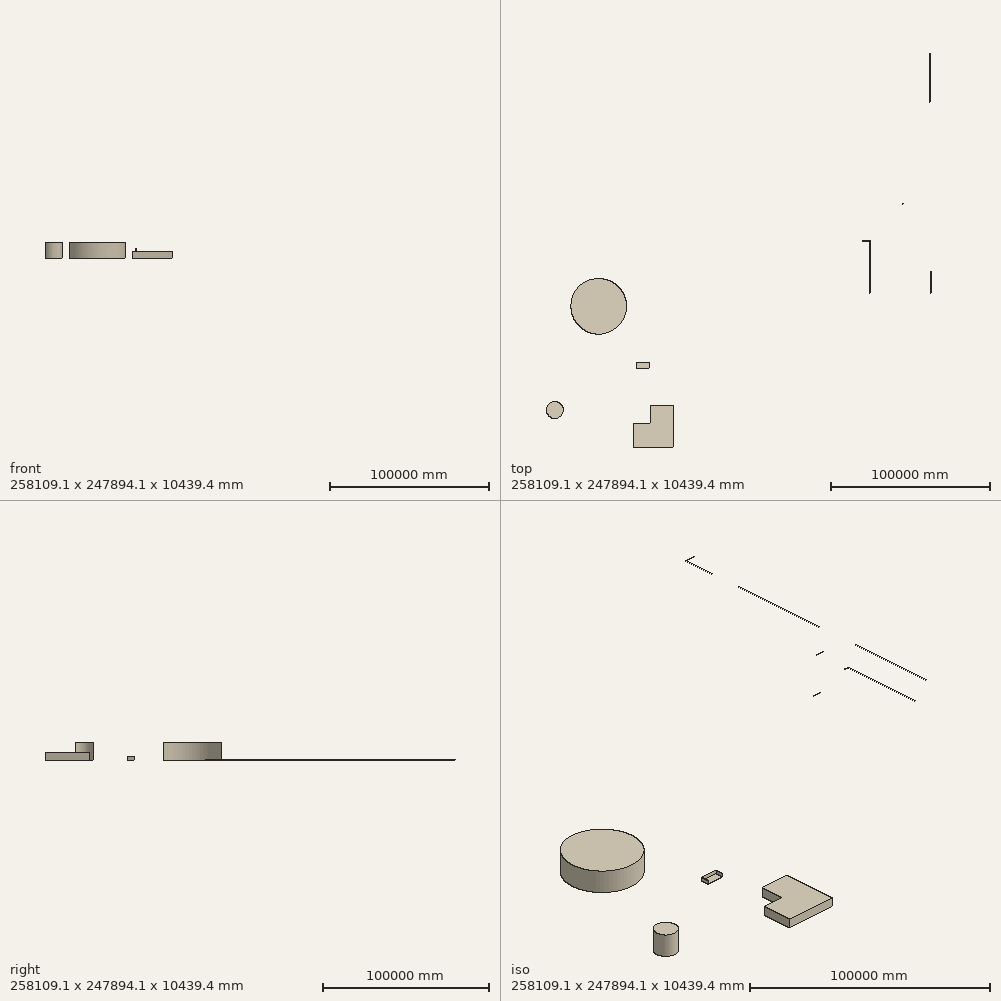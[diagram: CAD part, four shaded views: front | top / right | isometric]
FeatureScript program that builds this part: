
annotation { "Feature Type Name" : "Feature", "Feature Type Description" : "" }
export const myFeature = defineFeature(function(context is Context, id is Id, definition is map)
    precondition{}
    {
        {
            var Q0;
            Q0=qCreatedBy(makeId("Top.planeOp"),FACE);
            var sketch = newSketch(context, id + "F0", { "sketchPlane" : qUnion([Q0])});
            skCircle(sketch, "E0", {"center": v(-50054.64, -23220.98) * mm, "radius": 5334 * mm});
            skCircle(sketch, "E1", {"center": v(-35519.36, -23220.98) * mm, "radius": 5334 * mm});
            skCircle(sketch, "E2", {"center": v(-21108.4, -23220.98) * mm, "radius": 5334 * mm});
            skLineSegment(sketch, "E3", {"start": v(-70389.93, -5352.59) * mm, "end": v(-70389.93, -40568.15) * mm});
            skLineSegment(sketch, "E4", {"start": v(-68865.93, -3828.59) * mm, "end": v(-2745.86, -3828.59) * mm});
            skLineSegment(sketch, "E5", {"start": v(-1222.92, -5409.41) * mm, "end": v(-2607.68, -42521) * mm});
            skLineSegment(sketch, "E6", {"start": v(-68910.55, -42091.5) * mm, "end": v(-4175.24, -43987.52) * mm});
            skPoint(sketch, "E7.visualSharp", {"position": v(-70389.93, -3828.59) * mm});
            skArc(sketch, "E7.filletArc", {"start": v(-68865.93, -3828.59) * mm, "mid": v(-69943.56, -4274.96) * mm, "end": v(-70389.93, -5352.59) * mm});
            skPoint(sketch, "E8.visualSharp", {"position": v(-70389.93, -42048.17) * mm});
            skArc(sketch, "E8.filletArc", {"start": v(-70389.93, -40568.15) * mm, "mid": v(-69959.22, -41629.9) * mm, "end": v(-68910.55, -42091.5) * mm});
            skPoint(sketch, "E9.visualSharp", {"position": v(-2664.05, -44031.78) * mm});
            skArc(sketch, "E9.filletArc", {"start": v(-4175.24, -43987.52) * mm, "mid": v(-3089.45, -43577.07) * mm, "end": v(-2607.68, -42521) * mm});
            skPoint(sketch, "E10.visualSharp", {"position": v(-1163.93, -3828.59) * mm});
            skArc(sketch, "E10.filletArc", {"start": v(-1222.92, -5409.41) * mm, "mid": v(-1648.32, -4295.24) * mm, "end": v(-2745.86, -3828.59) * mm});
            skLineSegment(sketch, "E11", {"start": v(-50011.35, 72049.65) * mm, "end": v(-50011.35, 14325.6) * mm});
            skLineSegment(sketch, "E12", {"start": v(-50011.35, 14325.6) * mm, "end": v(35090.4, 14325.6) * mm});
            skLineSegment(sketch, "E13", {"start": v(35090.4, 14325.6) * mm, "end": v(35090.4, 75018.32) * mm});
            skLineSegment(sketch, "E14", {"start": v(35090.4, 75018.32) * mm, "end": v(27173.95, 75018.32) * mm});
            skLineSegment(sketch, "E15", {"start": v(27173.95, 75018.32) * mm, "end": v(27173.95, 93160.17) * mm});
            skLineSegment(sketch, "E16", {"start": v(27173.95, 93160.17) * mm, "end": v(-3007.48, 93160.17) * mm});
            skLineSegment(sketch, "E17", {"start": v(-3007.48, 93160.17) * mm, "end": v(-3007.48, 72049.65) * mm});
            skLineSegment(sketch, "E18", {"start": v(-3007.48, 72049.65) * mm, "end": v(-50011.35, 72049.65) * mm});
            skLineSegment(sketch, "E19.bottom", {"start": v(-57326.54, 5607.47) * mm, "end": v(41719.62, 5607.47) * mm});
            skLineSegment(sketch, "E19.top", {"start": v(-11431.89, 100338.75) * mm, "end": v(41719.62, 100338.75) * mm});
            skLineSegment(sketch, "E19.left", {"start": v(-57326.54, 5607.47) * mm, "end": v(-57326.54, 78356.48) * mm});
            skLineSegment(sketch, "E19.right", {"start": v(41719.62, 5607.47) * mm, "end": v(41719.62, 100338.75) * mm});
            skLineSegment(sketch, "E20", {"start": v(-11431.89, 100338.75) * mm, "end": v(-11431.89, 78356.48) * mm});
            skLineSegment(sketch, "E21", {"start": v(-11431.89, 78356.48) * mm, "end": v(-57326.54, 78356.48) * mm});
            skLineSegment(sketch, "E22", {"start": v(24636.78, -20086.42) * mm, "end": v(24636.78, -46694.1) * mm});
            skLineSegment(sketch, "E23", {"start": v(24636.78, -46694.1) * mm, "end": v(-445.33, -46694.1) * mm});
            skLineSegment(sketch, "E24", {"start": v(-445.33, -46694.1) * mm, "end": v(-445.33, -31842.26) * mm});
            skLineSegment(sketch, "E25", {"start": v(-445.33, -31842.26) * mm, "end": v(10009.28, -31842.26) * mm});
            skLineSegment(sketch, "E26", {"start": v(10009.28, -31842.26) * mm, "end": v(10009.28, -20086.42) * mm});
            skLineSegment(sketch, "E27", {"start": v(10009.28, -20086.42) * mm, "end": v(24636.78, -20086.42) * mm});
            skCircle(sketch, "E28", {"center": v(-22491.29, 42056.2) * mm, "radius": 17526 * mm});
            skLineSegment(sketch, "E29", {"start": v(-3866.35, 22739.19) * mm, "end": v(-2452.96, 22739.19) * mm});
            skLineSegment(sketch, "E30", {"start": v(-2452.96, 22739.19) * mm, "end": v(-2452.96, 6885.65) * mm});
            skLineSegment(sketch, "E31", {"start": v(-2452.96, 6885.65) * mm, "end": v(-3866.35, 6885.65) * mm});
            skLineSegment(sketch, "E32", {"start": v(-3866.35, 6885.65) * mm, "end": v(-3866.35, 9176.13) * mm});
            skLineSegment(sketch, "E33", {"start": v(-3866.35, 9176.13) * mm, "end": v(-55251.57, 10052.83) * mm});
            skLineSegment(sketch, "E34", {"start": v(-55251.57, 10052.83) * mm, "end": v(-55223.3, 11709.27) * mm});
            skLineSegment(sketch, "E35", {"start": v(-55223.3, 11709.27) * mm, "end": v(-3866.35, 10833.05) * mm});
            skLineSegment(sketch, "E36", {"start": v(-3866.35, 10833.05) * mm, "end": v(-3866.35, 22739.19) * mm});
            skSolve(sketch);
        }
        {
            var Q0;
            Q0=makeQuery(id+"F0.imprint","IMPRINT",FACE,{"disambiguationData":[TD([[makeQuery(id+"F0.imprint","IMPRINT",EDGE,{"derivedFrom":sQuery(id+"F0.wireOp",EDGE,"E28")}),1.0]])]});
            extrude(context, id + "F1", {"entities" : qUnion([Q0]), "depth" : 10363.2 * mm});
        }
        {
            var Q0;
            Q0=makeQuery(id+"F0.imprint","IMPRINT",FACE,{"disambiguationData":[TD([[makeQuery(id+"F0.imprint","IMPRINT",EDGE,{"derivedFrom":sQuery(id+"F0.wireOp",EDGE,"E0")}),1.0]])]});
            extrude(context, id + "F2", {"entities" : qUnion([Q0]), "depth" : 10363.2 * mm});
        }
        {
            var Q0;
            Q0=makeQuery(id+"F0.imprint","IMPRINT",FACE,{"disambiguationData":[TD([[makeQuery(id+"F0.imprint","IMPRINT",EDGE,{"derivedFrom":sQuery(id+"F0.wireOp",EDGE,"E22")}),-1.0]])]});
            extrude(context, id + "F3", {"entities" : qUnion([Q0]), "depth" : 4267.2 * mm});
        }
        {
            var Q0;
            Q0=qCreatedBy(makeId("Top.planeOp"),FACE);
            var sketch = newSketch(context, id + "F4", { "sketchPlane" : qUnion([Q0])});
            skPoint(sketch, "E37.0", {"position": v(-445.33, -31842.26) * mm});
            skLineSegment(sketch, "E38.0", {"start": v(-445.33, -46694.1) * mm, "end": v(-445.33, -31842.26) * mm});
            skLineSegment(sketch, "E39", {"start": v(-2274.13, -53883.38) * mm, "end": v(-2274.13, 12541.85) * mm, "construction": true});
            skLineSegment(sketch, "E40.0", {"start": v(-57326.54, 5607.47) * mm, "end": v(41719.62, 5607.47) * mm});
            skPoint(sketch, "E41", {"position": v(-2274.13, 5607.47) * mm});
            skPoint(sketch, "E42", {"position": v(-2274.13, -4450.93) * mm});
            skPoint(sketch, "E43", {"position": v(-2274.13, -10546.93) * mm});
            skPoint(sketch, "E44", {"position": v(-2274.13, -16642.93) * mm});
            skPoint(sketch, "E45", {"position": v(-2274.13, -22738.93) * mm});
            skPoint(sketch, "E46", {"position": v(-2274.13, -28834.93) * mm});
            skPoint(sketch, "E47", {"position": v(-2274.13, -34930.93) * mm});
            skPoint(sketch, "E48", {"position": v(-2274.13, -41026.93) * mm});
            skSolve(sketch);
        }
        {
            var Q0;
            Q0=qCreatedBy(makeId("Top.planeOp"),FACE);
            var sketch = newSketch(context, id + "F5", { "sketchPlane" : qUnion([Q0])});
            skLineSegment(sketch, "E49.bottom", {"start": v(1425.92, -198.16) * mm, "end": v(1629.12, -198.16) * mm});
            skLineSegment(sketch, "E49.top", {"start": v(1425.92, -401.36) * mm, "end": v(1629.12, -401.36) * mm});
            skLineSegment(sketch, "E49.left", {"start": v(1425.92, -198.16) * mm, "end": v(1425.92, -210.86) * mm});
            skLineSegment(sketch, "E49.right", {"start": v(1629.12, -198.16) * mm, "end": v(1629.12, -210.86) * mm});
            skLineSegment(sketch, "E50", {"start": v(1425.92, -210.86) * mm, "end": v(1521.17, -210.86) * mm});
            skLineSegment(sketch, "E51", {"start": v(1425.92, -388.66) * mm, "end": v(1521.17, -388.66) * mm});
            skLineSegment(sketch, "E52", {"start": v(1527.52, -210.86) * mm, "end": v(1527.52, -388.66) * mm, "construction": true});
            skLineSegment(sketch, "E53", {"start": v(1521.17, -210.86) * mm, "end": v(1521.17, -388.66) * mm});
            skLineSegment(sketch, "E54", {"start": v(1533.87, -210.86) * mm, "end": v(1533.87, -388.66) * mm});
            skPoint(sketch, "E55", {"position": v(1527.52, -210.86) * mm});
            skLineSegment(sketch, "E56.trimOffspring", {"start": v(1425.92, -388.66) * mm, "end": v(1425.92, -401.36) * mm});
            skLineSegment(sketch, "E57.trimOffspring", {"start": v(1629.12, -388.66) * mm, "end": v(1629.12, -401.36) * mm});
            skLineSegment(sketch, "E58.trimOffspring", {"start": v(1533.87, -210.86) * mm, "end": v(1629.12, -210.86) * mm});
            skLineSegment(sketch, "E59.trimOffspring", {"start": v(1533.87, -388.66) * mm, "end": v(1629.12, -388.66) * mm});
            skSolve(sketch);
        }
        {
            var Q0;
            Q0 = qSketchRegion(id + "F5", true);
            extrude(context, id + "F6", {"entities" : qUnion([Q0]), "depth" : 6705.6 * mm});
        }
        {
            var Q0;
            Q0=qCreatedBy(makeId("Top.planeOp"),FACE);
            var sketch = newSketch(context, id + "F7", { "sketchPlane" : qUnion([Q0])});
            skLineSegment(sketch, "E60.bottom", {"start": v(9761.53, 3051.6) * mm, "end": v(1227.13, 3051.6) * mm});
            skLineSegment(sketch, "E60.top", {"start": v(9761.53, 7014) * mm, "end": v(1227.13, 7014) * mm});
            skLineSegment(sketch, "E60.left", {"start": v(9761.53, 3051.6) * mm, "end": v(9761.53, 7014) * mm});
            skLineSegment(sketch, "E60.right", {"start": v(1227.13, 3051.6) * mm, "end": v(1227.13, 7014) * mm});
            skSolve(sketch);
        }
        {
            var Q0;
            Q0=makeQuery(id+"F7.imprint","IMPRINT",FACE,{"disambiguationData":[TD([[makeQuery(id+"F7.imprint","IMPRINT",EDGE,{"derivedFrom":sQuery(id+"F7.wireOp",EDGE,"E60.bottom")}),-1.0]])]});
            extrude(context, id + "F8", {"entities" : qUnion([Q0]), "depth" : 1828.8 * mm});
        }
        {
            var Q0;
            Q0=makeQuery(id+"F8.opExtrude","CAP_FACE",FACE,{"disambiguationData":[OSD([sQuery(id+"F7.wireOp",EDGE,"E60.bottom"),sQuery(id+"F7.wireOp",EDGE,"E60.top"),sQuery(id+"F7.wireOp",EDGE,"E60.left"),sQuery(id+"F7.wireOp",EDGE,"E60.right")])],"isStart":false});
            var Q1;
            Q1=makeQuery(id+"F8.opExtrude","SWEPT_FACE",FACE,{"disambiguationData":[OSD([sQuery(id+"F7.wireOp",EDGE,"E60.bottom")])]});
            shell(context, id + "F9", {"entities" : qUnion([Q0, Q1]), "thickness" : 152.4 * mm});
        }
        {
            var Q0;
            Q0=qCreatedBy(makeId("Top.planeOp"),FACE);
            var sketch = newSketch(context, id + "F10", { "sketchPlane" : qUnion([Q0])});
            skLineSegment(sketch, "E61", {"start": v(-4958.39, 41069.14) * mm, "end": v(0, 41069.14) * mm});
            skLineSegment(sketch, "E62", {"start": v(0, 41069.14) * mm, "end": v(0, 5647.02) * mm});
            skLineSegment(sketch, "E63", {"start": v(-1768.76, 5694.65) * mm, "end": v(-1768.76, -50952.97) * mm});
            skLineSegment(sketch, "E64", {"start": v(-60956.88, -51634.85) * mm, "end": v(90083.05, -50952.97) * mm});
            skLineSegment(sketch, "E65", {"start": v(90083.05, -50952.97) * mm, "end": v(90158.65, -67698.56) * mm});
            skLineSegment(sketch, "E66", {"start": v(143293.73, 83296.76) * mm, "end": v(148252.12, 83296.76) * mm});
            skLineSegment(sketch, "E67", {"start": v(148252.12, 83296.76) * mm, "end": v(148252.12, 50008.24) * mm});
            skLineSegment(sketch, "E68", {"start": v(158615.25, 106655.85) * mm, "end": v(158615.25, 50008.24) * mm});
            skLineSegment(sketch, "E69", {"start": v(186656.7, 50008.24) * mm, "end": v(185974.83, 201048.17) * mm});
            skLineSegment(sketch, "E70", {"start": v(185974.83, 201048.17) * mm, "end": v(202720.42, 201123.77) * mm});
            skLineSegment(sketch, "E71", {"start": v(162577.64, 50008.24) * mm, "end": v(162475.86, 72551.32) * mm});
            skLineSegment(sketch, "E72", {"start": v(168955.34, 106351.05) * mm, "end": v(168955.34, 90196.65) * mm});
            skLineSegment(sketch, "E73", {"start": v(170479.34, 89891.85) * mm, "end": v(169260.14, 89891.85) * mm});
            skLineSegment(sketch, "E74", {"start": v(170784.14, 89587.05) * mm, "end": v(170784.14, 50008.24) * mm});
            skPoint(sketch, "E75.visualSharp", {"position": v(168955.34, 89891.85) * mm});
            skArc(sketch, "E75.filletArc", {"start": v(168955.34, 90196.65) * mm, "mid": v(169044.61, 89981.13) * mm, "end": v(169260.14, 89891.85) * mm});
            skPoint(sketch, "E76.visualSharp", {"position": v(170784.14, 89891.85) * mm});
            skArc(sketch, "E76.filletArc", {"start": v(170784.14, 89587.05) * mm, "mid": v(170694.86, 89802.58) * mm, "end": v(170479.34, 89891.85) * mm});
            skLineSegment(sketch, "E77", {"start": v(169260.14, 106655.85) * mm, "end": v(173525.96, 106655.85) * mm});
            skLineSegment(sketch, "E78", {"start": v(173830.76, 106962.03) * mm, "end": v(173828, 107571.62) * mm});
            skPoint(sketch, "E79.visualSharp", {"position": v(168955.34, 106655.85) * mm});
            skArc(sketch, "E79.filletArc", {"start": v(169260.14, 106655.85) * mm, "mid": v(169044.61, 106566.58) * mm, "end": v(168955.34, 106351.05) * mm});
            skPoint(sketch, "E80.visualSharp", {"position": v(173832.14, 106655.85) * mm});
            skArc(sketch, "E80.filletArc", {"start": v(173525.96, 106655.85) * mm, "mid": v(173741.97, 106745.61) * mm, "end": v(173830.76, 106962.03) * mm});
            skFitSpline(sketch, "E81", {"points": [v(202421.17, 51616.1) * mm, v(197611.3, 76949.33) * mm, v(204336.1, 81724.27) * mm, v(216581.6, 92586.88) * mm, v(207957.06, 110809.57) * mm, v(203640.85, 122149.6) * mm], "startDerivative": vector(-37792.28, 122645.94) * mm, "endDerivative": vector(-14828.4, 60020.42) * mm});
            skSolve(sketch);
        }
        {
            var Q0;
            Q0=sQuery(id+"F10.wireOp",EDGE,"E67");
            var Q1;
            Q1=sQuery(id+"F10.wireOp",VERTEX,"E67.end");
            cPlane(context, id + "F11", {"entities" : qUnion([Q0, Q1]), "cplaneType" : CPlaneType.LINE_POINT, "offset" : 25.4 * mm, "width" : 152.4 * mm, "height" : 152.4 * mm});
        }
        {
            var Q0;
            Q0=qCreatedBy(id+"F11.planeOp",FACE);
            var sketch = newSketch(context, id + "F12", { "sketchPlane" : qUnion([Q0])});
            skCircle(sketch, "E82", {"center": v(148252.12, 0) * mm, "radius": 76.2 * mm});
            skCircle(sketch, "E83", {"center": v(170784.14, 0) * mm, "radius": 76.2 * mm});
            skCircle(sketch, "E84", {"center": v(186656.7, 0) * mm, "radius": 76.2 * mm});
            skSolve(sketch);
        }
        {
            var Q0;
            Q0=makeQuery(id+"F12.imprint","IMPRINT",FACE,{"disambiguationData":[TD([[makeQuery(id+"F12.imprint","IMPRINT",EDGE,{"derivedFrom":sQuery(id+"F12.wireOp",EDGE,"E82")}),1.0]])]});
            var Q1;
            Q1=sQuery(id+"F10.wireOp",EDGE,"E67");
            var Q2;
            Q2=sQuery(id+"F10.wireOp",EDGE,"E66");
            sweep(context, id + "F13", {"profiles" : qUnion([Q0]), "path" : qUnion([Q1, Q2])});
        }
        {
            var Q0;
            Q0=makeQuery(id+"F12.imprint","IMPRINT",FACE,{"disambiguationData":[TD([[makeQuery(id+"F12.imprint","IMPRINT",EDGE,{"derivedFrom":sQuery(id+"F12.wireOp",EDGE,"E83")}),1.0]])]});
            var Q1;
            Q1=sQuery(id+"F10.wireOp",EDGE,"E74");
            var Q2;
            Q2=sQuery(id+"F10.wireOp",EDGE,"E76.filletArc");
            var Q3;
            Q3=sQuery(id+"F10.wireOp",EDGE,"E73");
            var Q4;
            Q4=sQuery(id+"F10.wireOp",EDGE,"E75.filletArc");
            var Q5;
            Q5=sQuery(id+"F10.wireOp",EDGE,"E72");
            var Q6;
            Q6=sQuery(id+"F10.wireOp",EDGE,"E79.filletArc");
            var Q7;
            Q7=sQuery(id+"F10.wireOp",EDGE,"E77");
            var Q8;
            Q8=sQuery(id+"F10.wireOp",EDGE,"E80.filletArc");
            var Q9;
            Q9=sQuery(id+"F10.wireOp",EDGE,"E78");
            sweep(context, id + "F14", {"profiles" : qUnion([Q0]), "path" : qUnion([Q1, Q2, Q3, Q4, Q5, Q6, Q7, Q8, Q9])});
        }
        {
            var Q0;
            Q0=makeQuery(id+"F12.imprint","IMPRINT",FACE,{"disambiguationData":[TD([[makeQuery(id+"F12.imprint","IMPRINT",EDGE,{"derivedFrom":sQuery(id+"F12.wireOp",EDGE,"E84")}),1.0]])]});
            var Q1;
            Q1=sQuery(id+"F10.wireOp",EDGE,"E69");
            var Q2;
            Q2=sQuery(id+"F10.wireOp",EDGE,"E70");
            sweep(context, id + "F15", {"profiles" : qUnion([Q0]), "path" : qUnion([Q1, Q2])});
        }
    });
